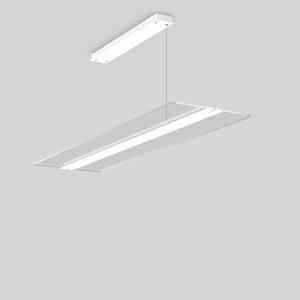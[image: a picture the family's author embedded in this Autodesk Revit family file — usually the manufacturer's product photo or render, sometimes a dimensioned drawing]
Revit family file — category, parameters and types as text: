
# Revit family: twindot_s_312263_002_dd94
name_source: partatom
category: Lighting Fixtures
units: mm (PartAtom-declared; Revit-internal decimal feet)

## family parameters
Cut with Voids When Loaded = No
Host = Face
Light Source = No
Part Type = Normal
Room Calculation Point = No
Round Connector Dimension = Use Diameter
Shared = No

## types (1)
- TWINDOT S (1 x LED Modul 830, 6500 lm, 3000)
    Apparent Load = 57 VA
    CIE Flux Codes = 47 77 94 55 100
    Color Rendering = 80
    Color Temperature = 3000
    Default Elevation = 1800 mm
    Description = Series: TWINDOT S
LED pendant luminaire with extremely flat and frameless appearance. Middle bar made of aluminium extrusion profile, powder-coated. Transparent light guide made of UV-resistant acrylic glass (PMMA) with TWINDOT prismatic. Light control with perfectly glare-free TWINDOT technology for pleasantly gentle light with soft shadows. Even and wide indirect and direct light distribution. Direct 55%, indirect 45% light emission. 4-point steel cable suspension, steplessly adjustable. Converter integrated in the canopy (powder-coated white). Power supply through suspension cable. 
Colour: traffic white, matt (RAL 9016)
Length: 1200 mm
Width: 350 mm
Height: 20 mm
Suspension length: 500-1200 mm
Lamp: LED
Socket: without socket
Colour temperature: 3000K
Colour rendering index (CRI): 80
System power: 57 W
Rated luminous flux: 6500 lm
Luminous efficiency: 114 lm/W
Control gear: Regulated power supply
Protection class: I
Type of protection: IP 20
    Height = 20 mm  [stored 0.0656168 ft]
    Lamp = 1 x LED Modul 830
    Lamp Light Flux = 6500 lm
    Lamp count = 1
    Length = 1200 mm
    Lifetime = 50000 h
    Luminous efficacy = 114 lm/W
    Manufacturer = RZB
    ModVariant = No
    Model = 312263.002
    Mounting Place = Ceiling
    Mounting Type = Pendant
    Number of Poles = 1
    OnlyDefault = Yes
    Power Factor = 1
    Product Name = TWINDOT S
    Product group = Pendant modular luminaires
    ProductGroupID = 906
    Protection Class = Protection class I
    Protection Degree = IP 20
    RLX_Detail_Level = 1
    RLX_Emergency_Light_Flux = 0 lm
    RLX_Emergency_Type = 0
    RLX_Emergency_Type_DB = No
    RlxData = <blob elided: 35305 chars, md5=dd3a4c08>
    Socket = socket
    Standby Power = 0 W
    System Light Flux = 6500 lm
    System Power = 57 W
    Type Comments = Product without accessories
    Type Image = 312263.002.jpg
    URL = http://relux.com
    VarID = ---
    Voltage = 230 V
    Voltage Range = 220-240 V
    Weight = 0.00 kg
    Width = 350 mm

note: [stored X ft] marks values corroborated as IEEE doubles in the binary element streams (Revit-internal decimal feet)

## geometry (parser evidence)
native form markers: Blend x4, Sweep x11
no freeform markers — native parametric forms only
